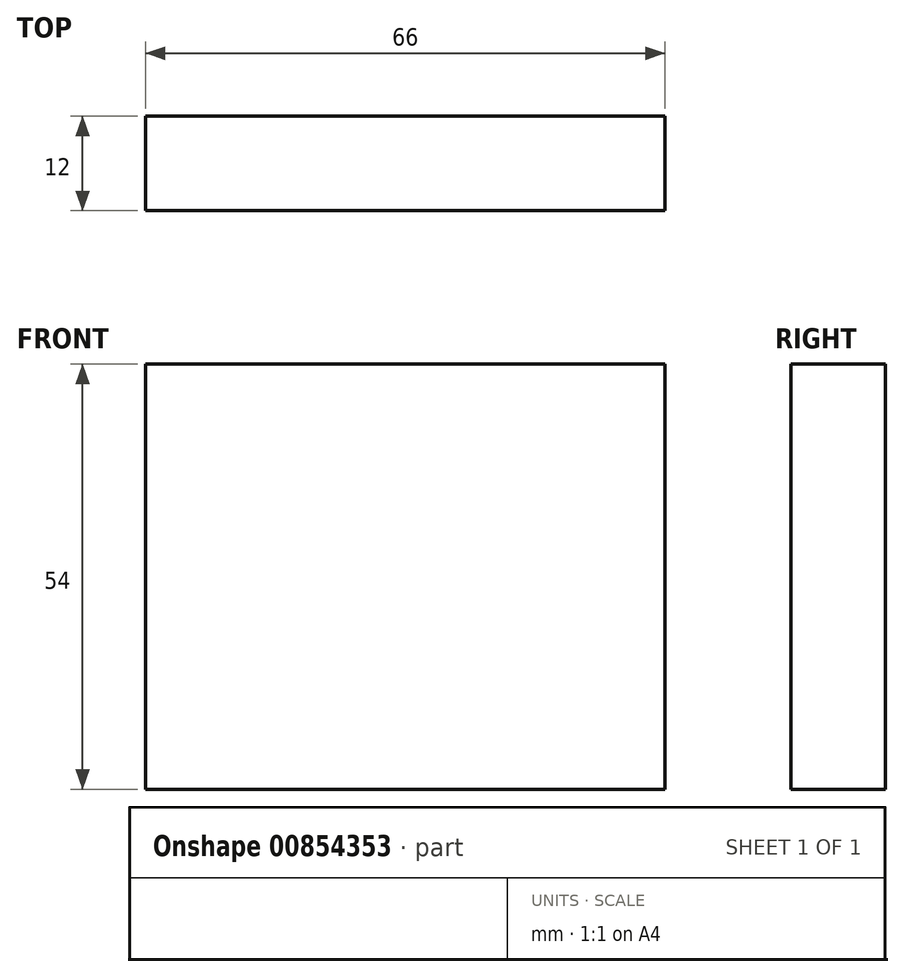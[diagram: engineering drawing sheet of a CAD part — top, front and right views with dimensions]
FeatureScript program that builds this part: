
annotation { "Feature Type Name" : "Feature", "Feature Type Description" : "" }
export const myFeature = defineFeature(function(context is Context, id is Id, definition is map)
    precondition{}
    {
        {
            var Q0;
            Q0=qCreatedBy(makeId("Front.planeOp"),FACE);
            var sketch = newSketch(context, id + "F0", { "sketchPlane" : qUnion([Q0])});
            skLineSegment(sketch, "E0.bottom", {"start": v(-101.44, 27) * mm, "end": v(108.56, 27) * mm});
            skLineSegment(sketch, "E0.top", {"start": v(-101.44, -27) * mm, "end": v(108.56, -27) * mm});
            skLineSegment(sketch, "E0.left", {"start": v(-101.44, 27) * mm, "end": v(-101.44, -27) * mm});
            skLineSegment(sketch, "E0.right", {"start": v(108.56, 27) * mm, "end": v(108.56, -27) * mm});
            skPoint(sketch, "E0.middle", {"position": v(3.56, 0) * mm});
            skSolve(sketch);
        }
        {
            var Q0;
            Q0 = qSketchRegion(id + "F0", true);
            extrude(context, id + "F1", {"entities" : qUnion([Q0]), "depth" : 12 * mm, "offsetDistance" : 25.4 * mm});
        }
        {
            var Q0;
            Q0=makeQuery(id+"F1.opExtrude","SWEPT_BODY",BODY,{"disambiguationData":[OSD([sQuery(id+"F0.wireOp",EDGE,"E0.bottom"),sQuery(id+"F0.wireOp",EDGE,"E0.top"),sQuery(id+"F0.wireOp",EDGE,"E0.left"),sQuery(id+"F0.wireOp",EDGE,"E0.right")])]});
            deleteBodies(context, id + "F2", {"entities" : qUnion([Q0])});
        }
        {
            var Q0;
            Q0=qCreatedBy(makeId("Front.planeOp"),FACE);
            var sketch = newSketch(context, id + "F3", { "sketchPlane" : qUnion([Q0])});
            skLineSegment(sketch, "E1.bottom", {"start": v(-45, 31.45) * mm, "end": v(45, 31.45) * mm});
            skLineSegment(sketch, "E1.top", {"start": v(-45, -36.55) * mm, "end": v(45, -36.55) * mm});
            skLineSegment(sketch, "E1.left", {"start": v(-45, 31.45) * mm, "end": v(-45, -36.55) * mm});
            skLineSegment(sketch, "E1.right", {"start": v(45, 31.45) * mm, "end": v(45, -36.55) * mm});
            skPoint(sketch, "E1.middle", {"position": v(0, -2.55) * mm});
            skSolve(sketch);
        }
        {
            var Q0;
            Q0 = qSketchRegion(id + "F3", true);
            extrude(context, id + "F4", {"entities" : qUnion([Q0]), "depth" : 12 * mm, "offsetDistance" : 25.4 * mm});
        }
        {
            var Q0;
            Q0=makeQuery(id+"F4.opExtrude","SWEPT_BODY",BODY,{"disambiguationData":[OSD([sQuery(id+"F3.wireOp",EDGE,"E1.bottom"),sQuery(id+"F3.wireOp",EDGE,"E1.top"),sQuery(id+"F3.wireOp",EDGE,"E1.left"),sQuery(id+"F3.wireOp",EDGE,"E1.right")])]});
            deleteBodies(context, id + "F5", {"entities" : qUnion([Q0])});
        }
        {
            var Q0;
            Q0=qCreatedBy(makeId("Front.planeOp"),FACE);
            var sketch = newSketch(context, id + "F6", { "sketchPlane" : qUnion([Q0])});
            skLineSegment(sketch, "E2.bottom", {"start": v(-45, 27) * mm, "end": v(45, 27) * mm});
            skLineSegment(sketch, "E2.top", {"start": v(-45, -27) * mm, "end": v(45, -27) * mm});
            skLineSegment(sketch, "E2.left", {"start": v(-45, 27) * mm, "end": v(-45, -27) * mm});
            skLineSegment(sketch, "E2.right", {"start": v(45, 27) * mm, "end": v(45, -27) * mm});
            skPoint(sketch, "E2.middle", {"position": v(0, 0) * mm});
            skSolve(sketch);
        }
        {
            var Q0;
            Q0 = qSketchRegion(id + "F6", true);
            extrude(context, id + "F7", {"entities" : qUnion([Q0]), "depth" : 12 * mm, "offsetDistance" : 25.4 * mm});
        }
        {
            var Q0;
            Q0=makeQuery(id+"F7.opExtrude","SWEPT_BODY",BODY,{"disambiguationData":[OSD([sQuery(id+"F6.wireOp",EDGE,"E2.bottom"),sQuery(id+"F6.wireOp",EDGE,"E2.top"),sQuery(id+"F6.wireOp",EDGE,"E2.left"),sQuery(id+"F6.wireOp",EDGE,"E2.right")])]});
            deleteBodies(context, id + "F8", {"entities" : qUnion([Q0])});
        }
        {
            var Q0;
            Q0=qCreatedBy(makeId("Front.planeOp"),FACE);
            var sketch = newSketch(context, id + "F9", { "sketchPlane" : qUnion([Q0])});
            skLineSegment(sketch, "E3.bottom", {"start": v(-33, 27) * mm, "end": v(33, 27) * mm});
            skLineSegment(sketch, "E3.top", {"start": v(-33, -27) * mm, "end": v(33, -27) * mm});
            skLineSegment(sketch, "E3.left", {"start": v(-33, 27) * mm, "end": v(-33, -27) * mm});
            skLineSegment(sketch, "E3.right", {"start": v(33, 27) * mm, "end": v(33, -27) * mm});
            skPoint(sketch, "E3.middle", {"position": v(0, 0) * mm});
            skSolve(sketch);
        }
        {
            var Q0;
            Q0 = qSketchRegion(id + "F9", true);
            extrude(context, id + "F10", {"entities" : qUnion([Q0]), "depth" : 12 * mm, "offsetDistance" : 25.4 * mm});
        }
    });
